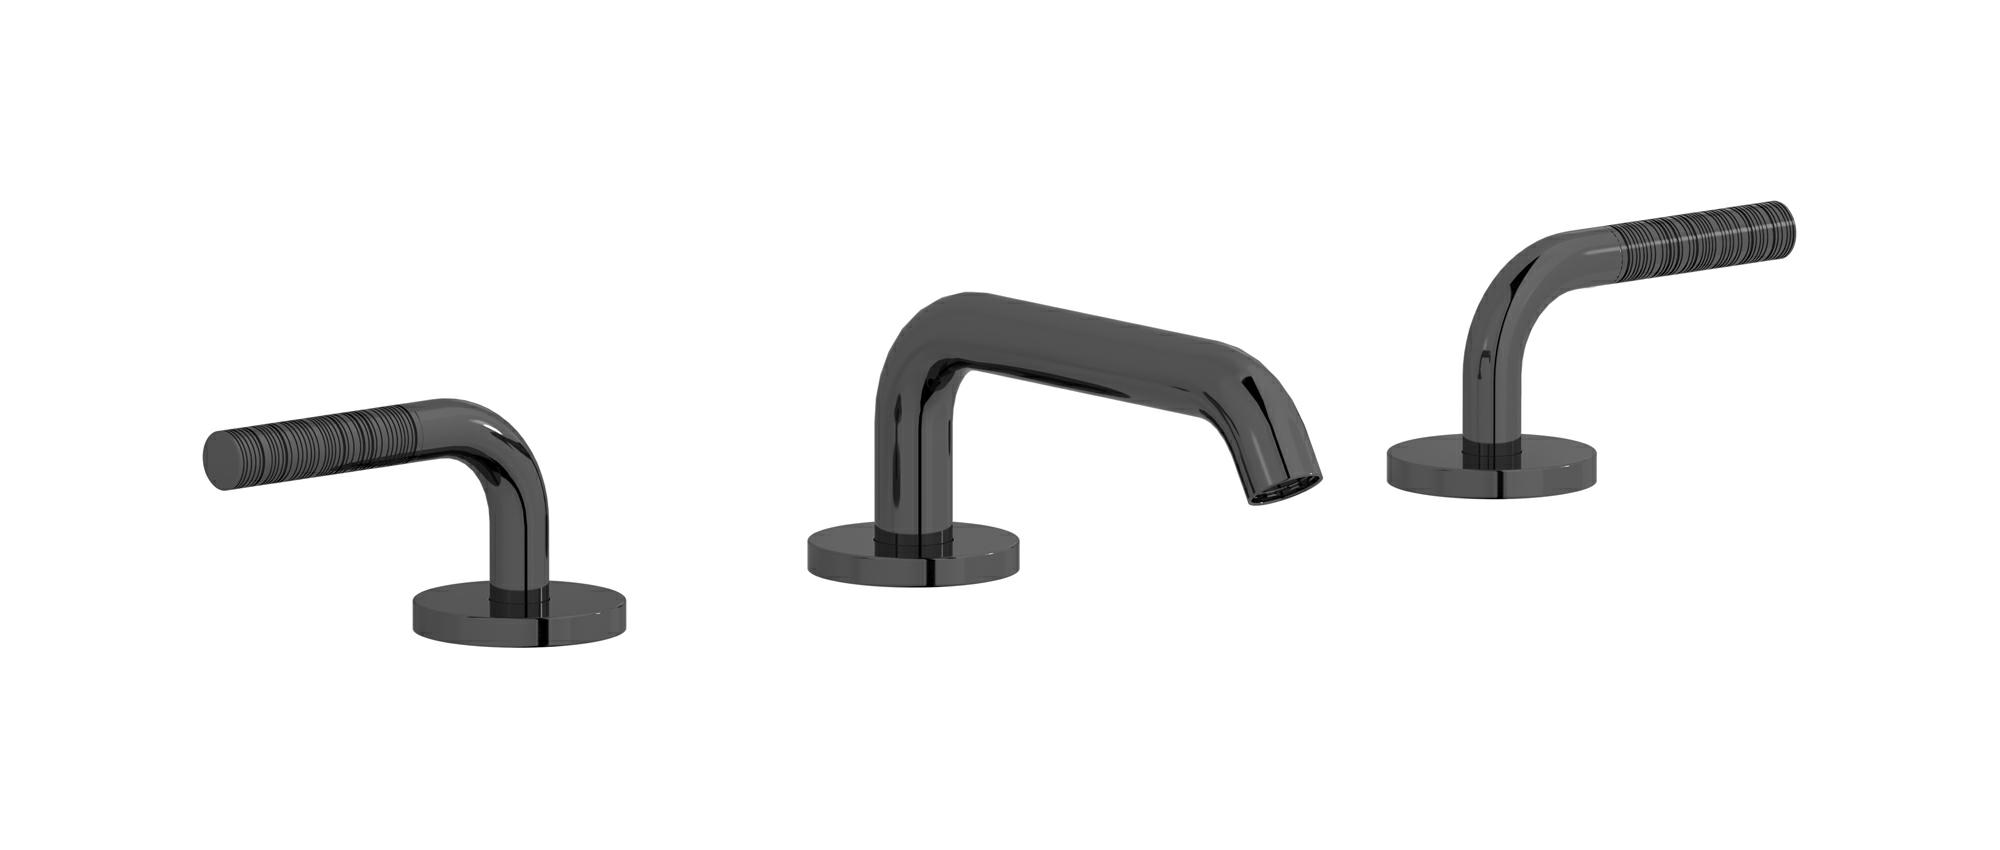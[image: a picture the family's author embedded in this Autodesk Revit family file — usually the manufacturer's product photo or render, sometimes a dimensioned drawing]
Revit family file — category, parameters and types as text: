
# Revit family: VN392
name_source: partatom
category: Apparecchi idraulici
units: mm (PartAtom-declared; Revit-internal decimal feet)

## family parameters
Basato su piano di lavoro = No
Condiviso = No
Mantieni orientamento annotazione = No
Numero OmniClass = 23.45.55.17
Punto di calcolo locali = No
Quota connettore circolare = Usa diametro
Sempre verticale = Sì
Taglio con vuoti quando caricato = No
Tipo di parte = Normale
Titolo OmniClass = Mixing Faucets

## types (12) — shared parameters
Cold water inlet = 10 mm  [stored 0.0328084 ft]
Commenti sul tipo = Three holes washbasin set with low spout
Connessione CW = No
Connessione HW = No
Connessione di scarico = No
Connessione di ventilazione = No
Descrizione = Three holes washbasin set with low spout
Hot water inlet = 10 mm  [stored 0.0328084 ft]
Produttore = IB Rubinetterie S.p.A.
URL = https://www.weareib.it
zero-valued in all types: Prospetto di default

## per-type parameters (varying)
| type | Finishes surface | Immagine tipo | Modello |
| Chrome | IB_Chrome | VN392CC.jpg | VN392CC |
| Black Chrome | IB_Black chrome | VN392CF.jpg | VN392CF |
| Brushed Black Chrome | IB_Brushed black chrome | VN392CS.jpg | VN392CS |
| Pale Gold | IB_Pale gold | VN392II.jpg | VN392II |
| Brushed Pale Gold | IB_brushed pale gold | VN392IS.jpg | VN392IS |
| Modern Bronze | IB_Modern bronze | VN392MB.jpg | VN392MB |
| Matt Black | IB_matt black | VN392NP.jpg | VN392NP |
| Gold | IB_gold | VN392OO.jpg | VN392OO |
| Brushed Gold | IB_brushed gold | VN392OS.jpg | VN392OS |
| Rose Gold | IB_Rose gold | VN392RS.jpg | VN392RS |
| Brushed Rose Gold | IB_Brushed rose gold | VN392SR.jpg | VN392SR |
| Brushed Nickel | IB_Brushed nickel | VN392SS.jpg | VN392SS |

note: [stored X ft] marks values corroborated as IEEE doubles in the binary element streams (Revit-internal decimal feet)
